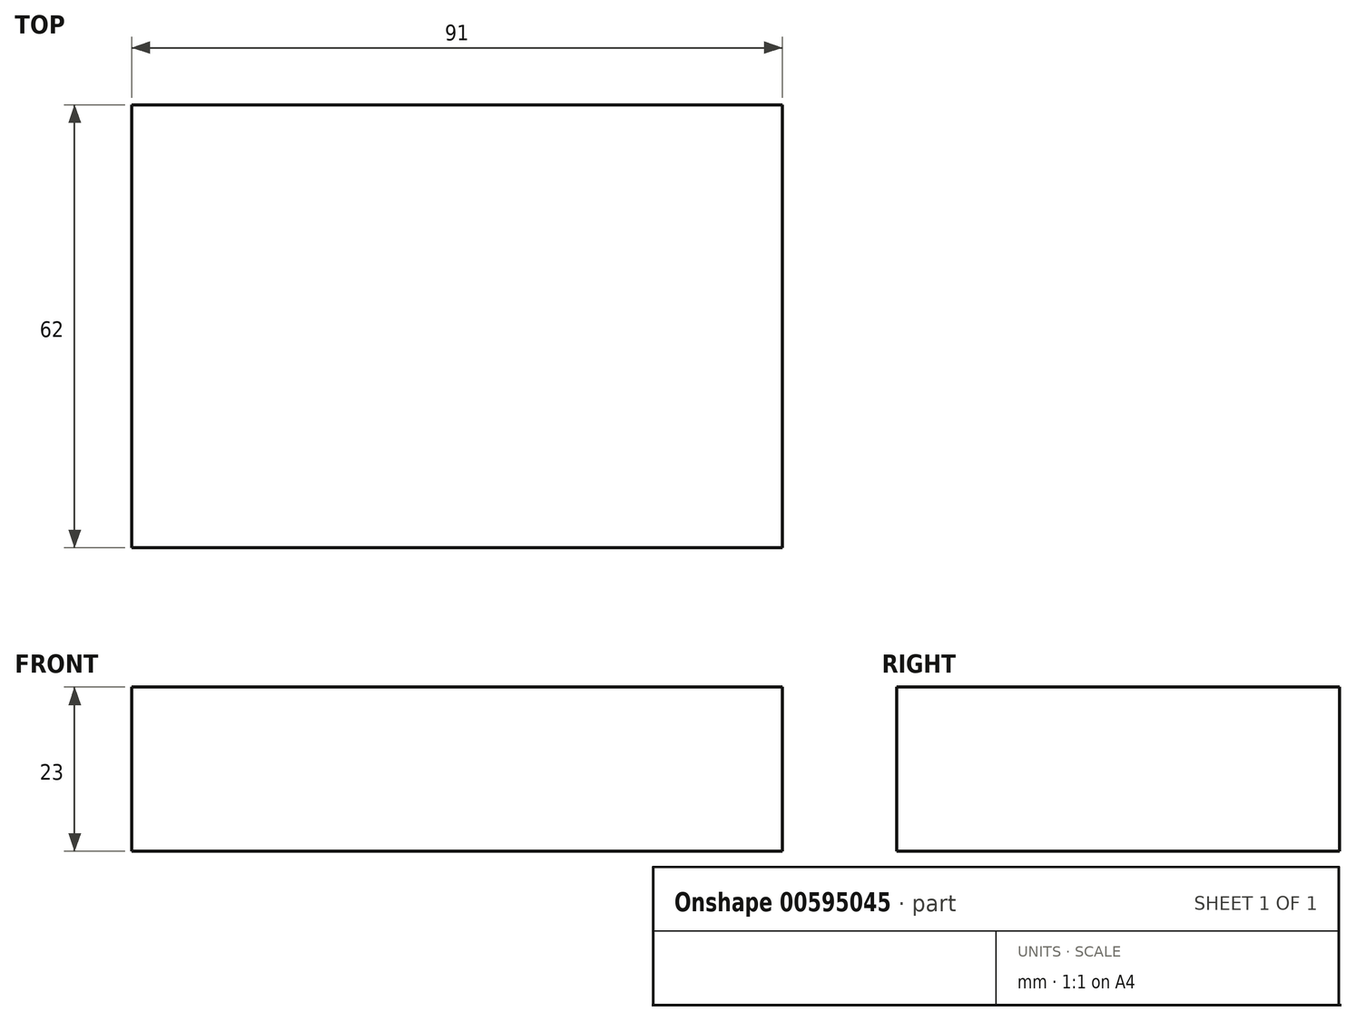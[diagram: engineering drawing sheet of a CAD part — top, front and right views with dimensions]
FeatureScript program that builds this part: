
annotation { "Feature Type Name" : "Feature", "Feature Type Description" : "" }
export const myFeature = defineFeature(function(context is Context, id is Id, definition is map)
    precondition{}
    {
        {
            var Q0;
            Q0=qCreatedBy(makeId("Top.planeOp"),FACE);
            var sketch = newSketch(context, id + "F0", { "sketchPlane" : qUnion([Q0])});
            skLineSegment(sketch, "E0.bottom", {"start": v(-42.5, 28) * mm, "end": v(42.5, 28) * mm});
            skLineSegment(sketch, "E0.top", {"start": v(-42.5, -28) * mm, "end": v(42.5, -28) * mm});
            skLineSegment(sketch, "E0.left", {"start": v(-42.5, 28) * mm, "end": v(-42.5, -28) * mm});
            skLineSegment(sketch, "E0.right", {"start": v(42.5, 28) * mm, "end": v(42.5, -28) * mm});
            skPoint(sketch, "E0.middle", {"position": v(0, 0) * mm});
            skLineSegment(sketch, "E1.0", {"start": v(-45.5, 31) * mm, "end": v(45.5, 31) * mm});
            skLineSegment(sketch, "E1.1", {"start": v(-45.5, 31) * mm, "end": v(-45.5, -31) * mm});
            skLineSegment(sketch, "E1.2", {"start": v(-45.5, -31) * mm, "end": v(45.5, -31) * mm});
            skLineSegment(sketch, "E1.3", {"start": v(45.5, 31) * mm, "end": v(45.5, -31) * mm});
            skSolve(sketch);
        }
        {
            var Q0;
            Q0=makeQuery(id+"F0.imprint","IMPRINT",FACE,{"disambiguationData":[TD([[makeQuery(id+"F0.imprint","IMPRINT",EDGE,{"derivedFrom":sQuery(id+"F0.wireOp",EDGE,"E0.bottom")}),-1.0]])]});
            var Q1;
            Q1=makeQuery(id+"F0.imprint","IMPRINT",FACE,{"disambiguationData":[TD([[makeQuery(id+"F0.imprint","IMPRINT",EDGE,{"derivedFrom":sQuery(id+"F0.wireOp",EDGE,"E0.bottom")}),1.0]])]});
            extrude(context, id + "F1", {"entities" : qUnion([Q0, Q1]), "depth" : 23 * mm, "offsetDistance" : 25 * mm});
        }
        {
            var Q0;
            Q0=makeQuery(id+"F1.opExtrude","SWEPT_BODY",BODY,{"disambiguationData":[OSD([sQuery(id+"F0.wireOp",EDGE,"E1.0"),sQuery(id+"F0.wireOp",EDGE,"E1.1"),sQuery(id+"F0.wireOp",EDGE,"E1.2"),sQuery(id+"F0.wireOp",EDGE,"E1.3")])]});
            transform(context, id + "F2", {"entities" : qUnion([Q0]), "transformType" : TransformType.TRANSLATION_3D, "dx" : 0 * mm, "dy" : 0 * mm, "dz" : 0 * mm, "makeCopy" : false});
        }
    });
